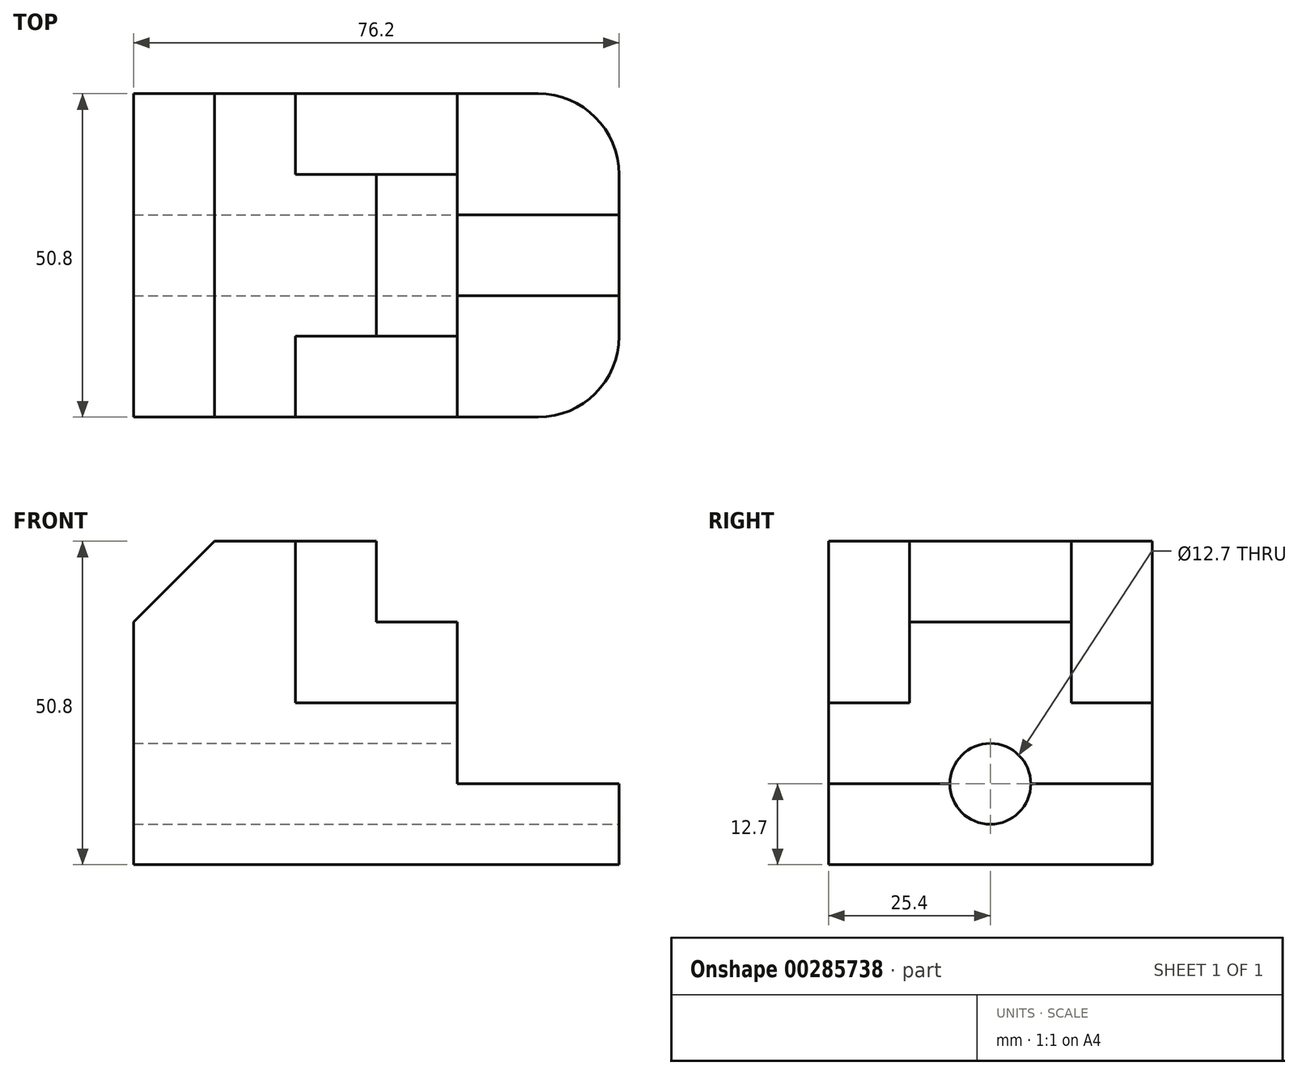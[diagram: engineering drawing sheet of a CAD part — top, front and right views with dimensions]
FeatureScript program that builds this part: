
annotation { "Feature Type Name" : "Feature", "Feature Type Description" : "" }
export const myFeature = defineFeature(function(context is Context, id is Id, definition is map)
    precondition{}
    {
        {
            var Q0;
            Q0=qCreatedBy(makeId("Front.planeOp"),FACE);
            var sketch = newSketch(context, id + "F0", { "sketchPlane" : qUnion([Q0])});
            skLineSegment(sketch, "E0", {"start": v(0, 0) * mm, "end": v(0, 38.1) * mm});
            skLineSegment(sketch, "E1", {"start": v(0, 38.1) * mm, "end": v(12.7, 50.8) * mm});
            skLineSegment(sketch, "E2", {"start": v(12.7, 50.8) * mm, "end": v(25.4, 50.8) * mm});
            skLineSegment(sketch, "E3", {"start": v(25.4, 50.8) * mm, "end": v(25.4, 25.4) * mm});
            skLineSegment(sketch, "E4", {"start": v(25.4, 25.4) * mm, "end": v(50.8, 25.4) * mm});
            skLineSegment(sketch, "E5", {"start": v(50.8, 25.4) * mm, "end": v(50.8, 12.7) * mm});
            skLineSegment(sketch, "E6", {"start": v(50.8, 12.7) * mm, "end": v(63.5, 12.7) * mm});
            skLineSegment(sketch, "E7", {"start": v(63.5, 12.7) * mm, "end": v(63.5, 0) * mm});
            skLineSegment(sketch, "E8", {"start": v(63.5, 0) * mm, "end": v(0, 0) * mm});
            skLineSegment(sketch, "E9", {"start": v(25.4, 50.8) * mm, "end": v(38.1, 50.8) * mm});
            skLineSegment(sketch, "E10", {"start": v(38.1, 50.8) * mm, "end": v(38.1, 38.1) * mm});
            skLineSegment(sketch, "E11", {"start": v(38.1, 38.1) * mm, "end": v(50.8, 38.1) * mm});
            skLineSegment(sketch, "E12", {"start": v(50.8, 38.1) * mm, "end": v(50.8, 25.4) * mm});
            skSolve(sketch);
        }
        {
            var Q0;
            Q0=makeQuery(id+"F0.imprint","IMPRINT",FACE,{"disambiguationData":[TD([[makeQuery(id+"F0.imprint","IMPRINT",EDGE,{"derivedFrom":sQuery(id+"F0.wireOp",EDGE,"E0")}),-1.0]])]});
            extrude(context, id + "F1", {"entities" : qUnion([Q0]), "endBound" : BoundingType.SYMMETRIC, "depth" : 50.8 * mm});
        }
        {
            var Q0;
            Q0=makeQuery(id+"F0.imprint","IMPRINT",FACE,{"disambiguationData":[TD([[makeQuery(id+"F0.imprint","IMPRINT",EDGE,{"derivedFrom":sQuery(id+"F0.wireOp",EDGE,"E3")}),1.0]])]});
            extrude(context, id + "F2", {"entities" : qUnion([Q0]), "operationType" : NewBodyOperationType.ADD, "endBound" : BoundingType.SYMMETRIC, "depth" : 25.4 * mm});
        }
        {
            var Q0;
            Q0=makeQuery(id+"F1.opExtrude","SWEPT_FACE",FACE,{"disambiguationData":[OSD([sQuery(id+"F0.wireOp",EDGE,"E6")])]});
            var sketch = newSketch(context, id + "F3", { "sketchPlane" : qUnion([Q0])});
            skLineSegment(sketch, "E13", {"start": v(76.2, 12.7) * mm, "end": v(76.2, -12.7) * mm});
            skArc(sketch, "E14", {"start": v(76.2, 12.7) * mm, "mid": v(72.48, 21.68) * mm, "end": v(63.5, 25.4) * mm});
            skArc(sketch, "E15", {"start": v(76.2, -12.7) * mm, "mid": v(72.48, -21.68) * mm, "end": v(63.5, -25.4) * mm});
            skLineSegment(sketch, "E16", {"start": v(63.5, 25.4) * mm, "end": v(63.5, -25.4) * mm});
            skSolve(sketch);
        }
        {
            var Q0;
            Q0 = qSketchRegion(id + "F3", true);
            extrude(context, id + "F4", {"entities" : qUnion([Q0]), "operationType" : NewBodyOperationType.ADD, "oppositeDirection" : true, "depth" : 12.7 * mm});
        }
        {
            var Q0;
            Q0=makeQuery(id+"F4.opExtrude","SWEPT_FACE",FACE,{"disambiguationData":[OSD([sQuery(id+"F3.wireOp",EDGE,"E13")])]});
            var sketch = newSketch(context, id + "F5", { "sketchPlane" : qUnion([Q0])});
            skCircle(sketch, "E17", {"center": v(0, 12.7) * mm, "radius": 6.35 * mm});
            skSolve(sketch);
        }
        {
            var Q0;
            Q0 = qSketchRegion(id + "F5", true);
            extrude(context, id + "F6", {"entities" : qUnion([Q0]), "operationType" : NewBodyOperationType.REMOVE, "endBound" : BoundingType.THROUGH_ALL, "oppositeDirection" : true, "depth" : 25.4 * mm});
        }
    });
